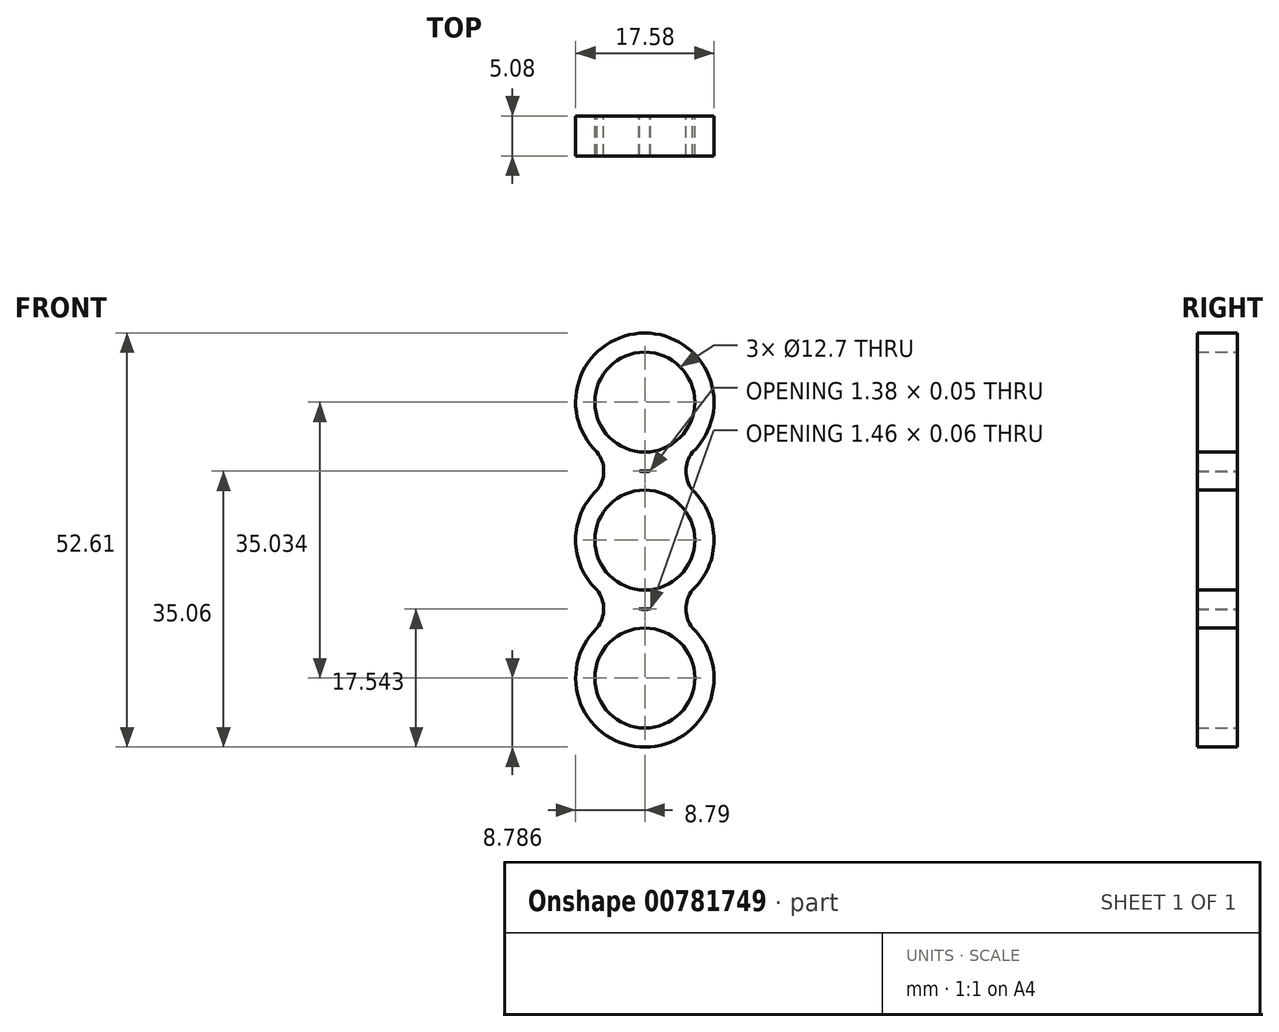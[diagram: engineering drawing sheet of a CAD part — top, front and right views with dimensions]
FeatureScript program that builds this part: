
annotation { "Feature Type Name" : "Feature", "Feature Type Description" : "" }
export const myFeature = defineFeature(function(context is Context, id is Id, definition is map)
    precondition{}
    {
        {
            var Q0;
            Q0=qCreatedBy(makeId("Front.planeOp"),FACE);
            var sketch = newSketch(context, id + "F0", { "sketchPlane" : qUnion([Q0])});
            skCircle(sketch, "E0", {"center": v(0, 0) * mm, "radius": 6.35 * mm});
            skCircle(sketch, "E1", {"center": v(0, 17.52) * mm, "radius": 6.35 * mm});
            skCircle(sketch, "E2", {"center": v(0, -17.51) * mm, "radius": 6.35 * mm});
            skLineSegment(sketch, "E3", {"start": v(0, -11.17) * mm, "end": v(0, -6.35) * mm});
            skLineSegment(sketch, "E4", {"start": v(0, 6.35) * mm, "end": v(0, 11.18) * mm});
            skCircle(sketch, "E5", {"center": v(0, 17.52) * mm, "radius": 8.79 * mm});
            skCircle(sketch, "E6", {"center": v(0, 0) * mm, "radius": 8.79 * mm});
            skCircle(sketch, "E7", {"center": v(0, -17.51) * mm, "radius": 8.79 * mm});
            skArc(sketch, "E8", {"start": v(-6.08, 6.35) * mm, "mid": v(-5.22, 8.76) * mm, "end": v(-6.08, 11.18) * mm});
            skArc(sketch, "E9", {"start": v(6.08, 11.18) * mm, "mid": v(5.21, 8.76) * mm, "end": v(6.08, 6.35) * mm});
            skArc(sketch, "E10", {"start": v(6.08, -6.35) * mm, "mid": v(5.22, -8.76) * mm, "end": v(6.08, -11.17) * mm});
            skArc(sketch, "E11", {"start": v(-6.08, -11.17) * mm, "mid": v(-5.22, -8.76) * mm, "end": v(-6.08, -6.35) * mm});
            skSolve(sketch);
        }
        {
            var Q0;
            Q0=makeQuery(id+"F0.imprint","IMPRINT",FACE,{"disambiguationData":[TD([[makeQuery(id+"F0.imprint","IMPRINT",EDGE,{"derivedFrom":sQuery(id+"F0.wireOp",EDGE,"E1")}),-1.0]])]});
            var Q1;
            {var subQ5=sQuery(id+"F0.wireOp",EDGE,"E0");var subQ9=sQuery(id+"F0.wireOp",EDGE,"E3");var subQ10=makeQuery(id+"F0.imprint","INTERSECT",VERTEX,{"derivedFrom":[subQ5,subQ9]});Q1=makeQuery(id+"F0.imprint","IMPRINT",FACE,{"disambiguationData":[TD([[makeQuery(id+"F0.imprint","IMPRINT",EDGE,{"disambiguationData":[TD([[subQ10,1.0]])],"derivedFrom":subQ5}),-1.0]])]});}
            var Q2;
            {var subQ8=sQuery(id+"F0.wireOp",EDGE,"E3");var subQ9=sQuery(id+"F0.wireOp",EDGE,"E0");var subQ10=makeQuery(id+"F0.imprint","INTERSECT",VERTEX,{"derivedFrom":[subQ9,subQ8]});Q2=makeQuery(id+"F0.imprint","IMPRINT",FACE,{"disambiguationData":[TD([[makeQuery(id+"F0.imprint","IMPRINT",EDGE,{"disambiguationData":[TD([[subQ10,-1.0]])],"derivedFrom":subQ9}),-1.0]])]});}
            var Q3;
            {var subQ0=sQuery(id+"F0.wireOp",EDGE,"E9");Q3=makeQuery(id+"F0.imprint","IMPRINT",FACE,{"disambiguationData":[TD([[makeQuery(id+"F0.imprint","IMPRINT",EDGE,{"derivedFrom":subQ0}),-1.0]])]});}
            var Q4;
            {var subQ0=sQuery(id+"F0.wireOp",EDGE,"E8");Q4=makeQuery(id+"F0.imprint","IMPRINT",FACE,{"disambiguationData":[TD([[makeQuery(id+"F0.imprint","IMPRINT",EDGE,{"derivedFrom":subQ0}),-1.0]])]});}
            var Q5;
            Q5=makeQuery(id+"F0.imprint","IMPRINT",FACE,{"disambiguationData":[TD([[makeQuery(id+"F0.imprint","IMPRINT",EDGE,{"derivedFrom":sQuery(id+"F0.wireOp",EDGE,"E2")}),-1.0]])]});
            var Q6;
            {var subQ0=sQuery(id+"F0.wireOp",EDGE,"E11");Q6=makeQuery(id+"F0.imprint","IMPRINT",FACE,{"disambiguationData":[TD([[makeQuery(id+"F0.imprint","IMPRINT",EDGE,{"derivedFrom":subQ0}),-1.0]])]});}
            var Q7;
            {var subQ0=sQuery(id+"F0.wireOp",EDGE,"E10");Q7=makeQuery(id+"F0.imprint","IMPRINT",FACE,{"disambiguationData":[TD([[makeQuery(id+"F0.imprint","IMPRINT",EDGE,{"derivedFrom":subQ0}),-1.0]])]});}
            extrude(context, id + "F1", {"entities" : qUnion([Q0, Q1, Q2, Q3, Q4, Q5, Q6, Q7]), "depth" : 5.08 * mm, "offsetDistance" : 25.4 * mm});
        }
    });
